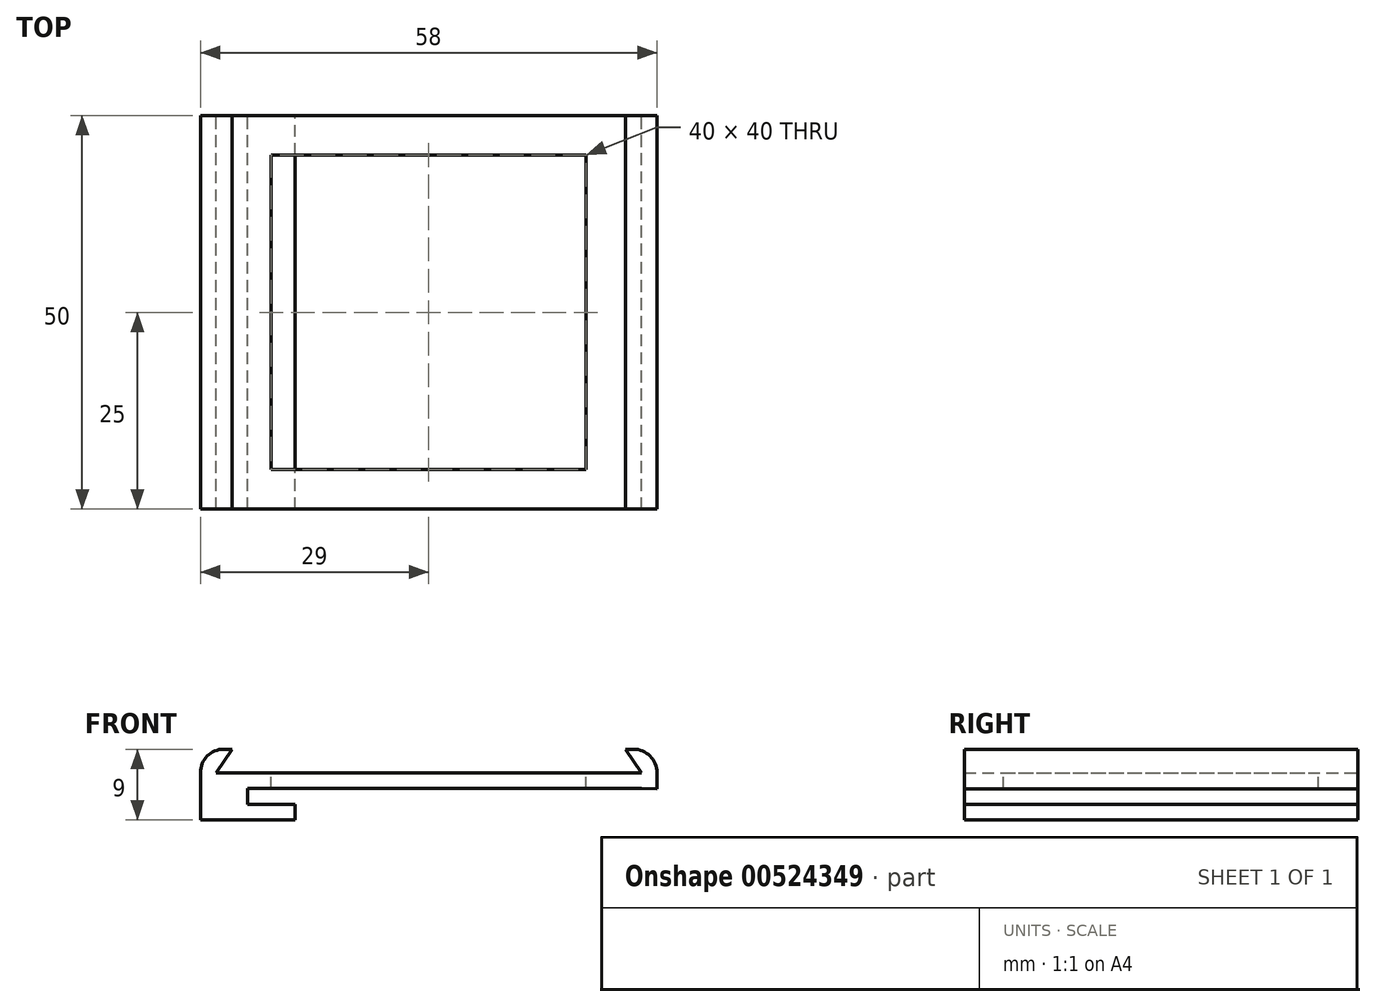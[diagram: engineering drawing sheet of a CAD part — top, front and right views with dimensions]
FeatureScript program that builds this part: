
annotation { "Feature Type Name" : "Feature", "Feature Type Description" : "" }
export const myFeature = defineFeature(function(context is Context, id is Id, definition is map)
    precondition{}
    {
        {
            var Q0;
            Q0=qCreatedBy(makeId("Front.planeOp"),FACE);
            var sketch = newSketch(context, id + "F0", { "sketchPlane" : qUnion([Q0])});
            skLineSegment(sketch, "E0", {"start": v(0, 6) * mm, "end": v(58, 6) * mm});
            skLineSegment(sketch, "E1", {"start": v(56, 4) * mm, "end": v(6, 4) * mm});
            skLineSegment(sketch, "E2", {"start": v(6, 4) * mm, "end": v(6, 2) * mm});
            skLineSegment(sketch, "E3", {"start": v(6, 2) * mm, "end": v(12, 2) * mm});
            skLineSegment(sketch, "E4", {"start": v(12, 2) * mm, "end": v(12, 0) * mm});
            skLineSegment(sketch, "E5", {"start": v(12, 0) * mm, "end": v(0, 0) * mm});
            skLineSegment(sketch, "E6", {"start": v(0, 0) * mm, "end": v(0, 6) * mm});
            skLineSegment(sketch, "E7", {"start": v(0, 6) * mm, "end": v(0, 9) * mm});
            skLineSegment(sketch, "E8", {"start": v(0, 9) * mm, "end": v(4, 9) * mm});
            skLineSegment(sketch, "E9", {"start": v(4, 9) * mm, "end": v(2, 6) * mm});
            skLineSegment(sketch, "E10", {"start": v(58, 6) * mm, "end": v(58, 9) * mm});
            skLineSegment(sketch, "E11", {"start": v(58, 9) * mm, "end": v(54, 9) * mm});
            skLineSegment(sketch, "E12", {"start": v(54, 9) * mm, "end": v(56, 6) * mm});
            skLineSegment(sketch, "E13", {"start": v(58, 6) * mm, "end": v(58, 3.96) * mm});
            skLineSegment(sketch, "E14", {"start": v(58, 3.96) * mm, "end": v(56, 4) * mm});
            skSolve(sketch);
        }
        {
            var Q0;
            Q0=qSketchRegion(id+"F0",true);
            extrude(context, id + "F1", {"entities" : qUnion([Q0]), "depth" : 50 * mm, "offsetDistance" : 25 * mm});
        }
        {
            var Q0;
            Q0=makeQuery(id+"F1.opExtrude","SWEPT_EDGE",EDGE,{"disambiguationData":[OSD([sQuery(id+"F0.wireOp",EDGE,"E7"),sQuery(id+"F0.wireOp",EDGE,"E8")])]});
            var Q1;
            Q1=makeQuery(id+"F1.opExtrude","SWEPT_EDGE",EDGE,{"disambiguationData":[OSD([sQuery(id+"F0.wireOp",EDGE,"E10"),sQuery(id+"F0.wireOp",EDGE,"E11")])]});
            fillet(context, id + "F2", {"entities" : qUnion([Q0, Q1]), "radius" : 3 * mm, "tangentPropagation" : true, "allowEdgeOverflow" : false});
        }
        {
            var Q0;
            Q0=makeQuery(id+"F1.opExtrude","SWEPT_FACE",FACE,{"disambiguationData":[OSD([sQuery(id+"F0.wireOp",EDGE,"E0")])]});
            var sketch = newSketch(context, id + "F3", { "sketchPlane" : qUnion([Q0])});
            skLineSegment(sketch, "E15.bottom", {"start": v(9, -45) * mm, "end": v(49, -45) * mm});
            skLineSegment(sketch, "E15.top", {"start": v(9, -5) * mm, "end": v(49, -5) * mm});
            skLineSegment(sketch, "E15.left", {"start": v(9, -45) * mm, "end": v(9, -5) * mm});
            skLineSegment(sketch, "E15.right", {"start": v(49, -45) * mm, "end": v(49, -5) * mm});
            skSolve(sketch);
        }
        {
            var Q0;
            Q0=makeQuery(id+"F3.imprint","IMPRINT",FACE,{"disambiguationData":[TD([[makeQuery(id+"F3.imprint","IMPRINT",EDGE,{"derivedFrom":sQuery(id+"F3.wireOp",EDGE,"E15.bottom")}),1.0]])]});
            extrude(context, id + "F4", {"entities" : qUnion([Q0]), "operationType" : NewBodyOperationType.REMOVE, "depth" : -2 * mm, "offsetDistance" : 25 * mm});
        }
    });
